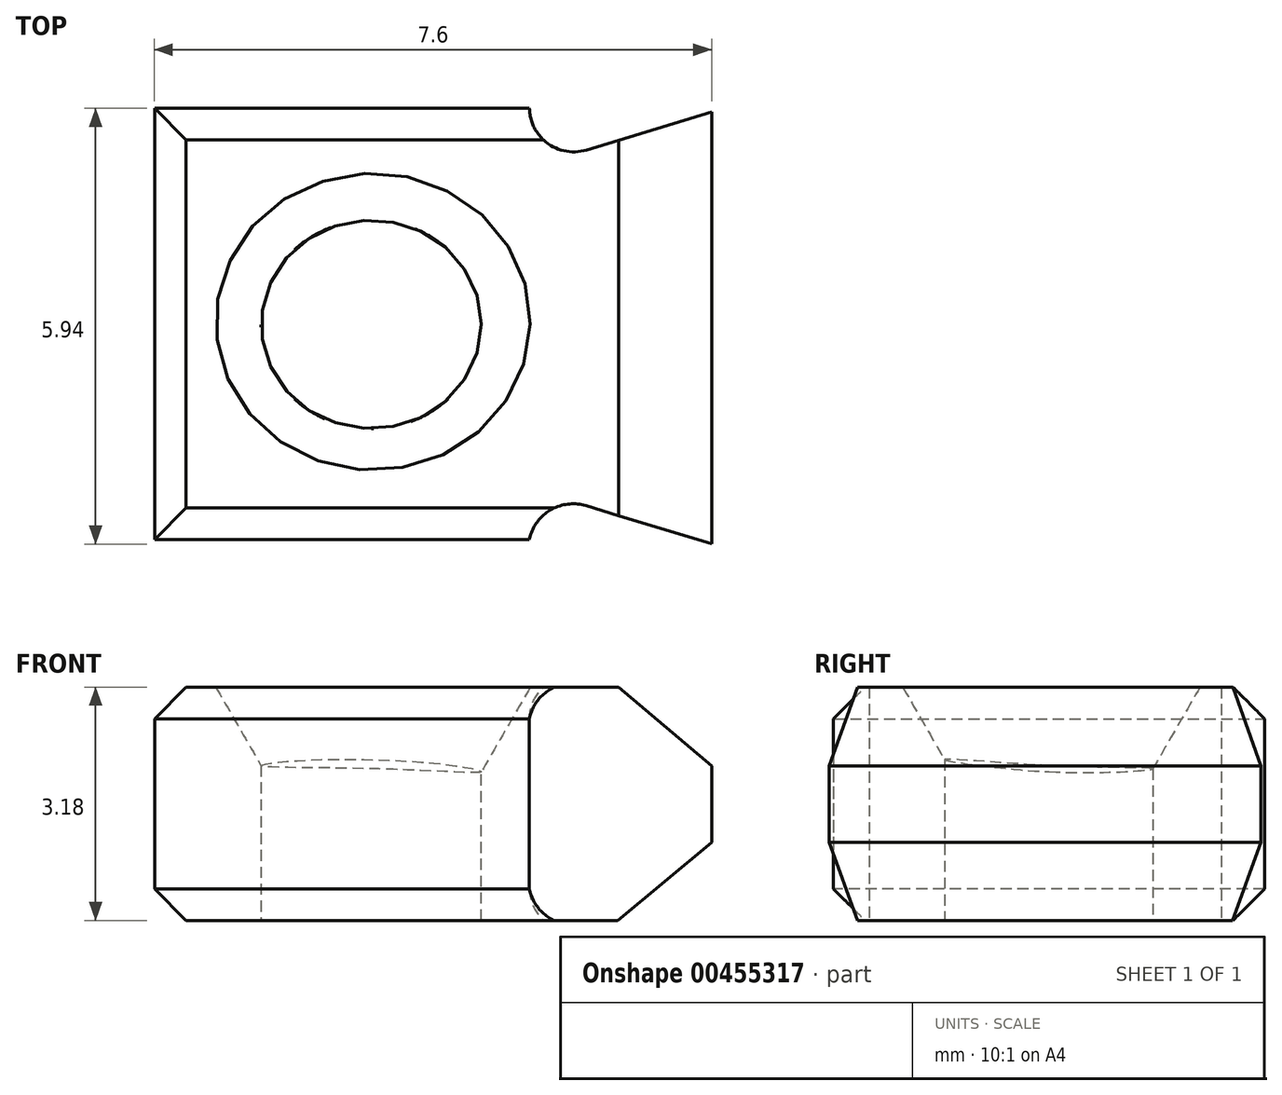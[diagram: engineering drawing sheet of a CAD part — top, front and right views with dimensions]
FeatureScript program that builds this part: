
annotation { "Feature Type Name" : "Feature", "Feature Type Description" : "" }
export const myFeature = defineFeature(function(context is Context, id is Id, definition is map)
    precondition{}
    {
        {
            var Q0;
            Q0=qCreatedBy(makeId("Top.planeOp"),FACE);
            var sketch = newSketch(context, id + "F0", { "sketchPlane" : qUnion([Q0])});
            skLineSegment(sketch, "E0.bottom", {"start": v(2.56, 2.94) * mm, "end": v(-2.56, 2.94) * mm});
            skLineSegment(sketch, "E0.top", {"start": v(2.56, -2.94) * mm, "end": v(-2.56, -2.94) * mm});
            skLineSegment(sketch, "E0.left", {"start": v(2.56, 2.94) * mm, "end": v(2.56, -2.94) * mm});
            skLineSegment(sketch, "E0.right", {"start": v(-2.56, 2.94) * mm, "end": v(-2.56, -2.94) * mm});
            skPoint(sketch, "E0.middle", {"position": v(0, 0) * mm});
            skLineSegment(sketch, "E1", {"start": v(5.04, 2.89) * mm, "end": v(5.04, -3) * mm});
            skLineSegment(sketch, "E2", {"start": v(5.04, 2.89) * mm, "end": v(3.34, 2.37) * mm});
            skLineSegment(sketch, "E3", {"start": v(5.04, -3) * mm, "end": v(3.32, -2.48) * mm});
            skArc(sketch, "E4", {"start": v(2.55, 2.94) * mm, "mid": v(2.8, 2.46) * mm, "end": v(3.34, 2.37) * mm});
            skArc(sketch, "E5", {"start": v(3.32, -2.48) * mm, "mid": v(2.84, -2.54) * mm, "end": v(2.56, -2.94) * mm});
            skSolve(sketch);
        }
        {
            var Q0;
            Q0=makeQuery(id+"F0.imprint","IMPRINT",FACE,{"disambiguationData":[TD([[makeQuery(id+"F0.imprint","IMPRINT",EDGE,{"derivedFrom":sQuery(id+"F0.wireOp",EDGE,"E0.bottom")}),1.0]])]});
            var Q1;
            Q1=makeQuery(id+"F0.imprint","IMPRINT",FACE,{"disambiguationData":[TD([[makeQuery(id+"F0.imprint","IMPRINT",EDGE,{"derivedFrom":sQuery(id+"F0.wireOp",EDGE,"E0.left")}),1.0]])]});
            extrude(context, id + "F1", {"entities" : qUnion([Q0, Q1]), "depth" : 3.18 * mm});
        }
        {
            var Q0;
            Q0=makeQuery(id+"F1.opExtrude","CAP_FACE",FACE,{"disambiguationData":[OSD([sQuery(id+"F0.wireOp",EDGE,"E0.bottom"),sQuery(id+"F0.wireOp",EDGE,"E0.top"),sQuery(id+"F0.wireOp",EDGE,"E0.right"),sQuery(id+"F0.wireOp",EDGE,"E1"),sQuery(id+"F0.wireOp",EDGE,"E2"),sQuery(id+"F0.wireOp",EDGE,"E3"),sQuery(id+"F0.wireOp",EDGE,"E4"),sQuery(id+"F0.wireOp",EDGE,"E5")])],"isStart":false});
            var sketch = newSketch(context, id + "F2", { "sketchPlane" : qUnion([Q0])});
            skEllipse(sketch, "E6", {"center": v(0.4, 0) * mm, "majorRadius": 1.5 * mm, "minorRadius": 1.42 * mm, "majorAxis": v(1, 0)});
            skSolve(sketch);
        }
        {
            var Q0;
            Q0=makeQuery(id+"F2.imprint","IMPRINT",FACE,{"disambiguationData":[TD([[makeQuery(id+"F2.imprint","IMPRINT",EDGE,{"derivedFrom":sQuery(id+"F2.wireOp",EDGE,"E6")}),1.0]])]});
            extrude(context, id + "F3", {"entities" : qUnion([Q0]), "operationType" : NewBodyOperationType.REMOVE, "endBound" : BoundingType.THROUGH_ALL, "oppositeDirection" : true, "depth" : 25 * mm});
        }
        {
            var Q0;
            Q0=makeQuery(id+"F1.opExtrude","CAP_FACE",FACE,{"disambiguationData":[OSD([sQuery(id+"F0.wireOp",EDGE,"E0.bottom"),sQuery(id+"F0.wireOp",EDGE,"E0.top"),sQuery(id+"F0.wireOp",EDGE,"E0.right"),sQuery(id+"F0.wireOp",EDGE,"E1"),sQuery(id+"F0.wireOp",EDGE,"E2"),sQuery(id+"F0.wireOp",EDGE,"E3"),sQuery(id+"F0.wireOp",EDGE,"E4"),sQuery(id+"F0.wireOp",EDGE,"E5")])],"isStart":false});
            var sketch = newSketch(context, id + "F4", { "sketchPlane" : qUnion([Q0])});
            skEllipse(sketch, "E7", {"center": v(0.42, 0.03) * mm, "majorRadius": 2.14 * mm, "minorRadius": 2.02 * mm, "majorAxis": v(1, 0)});
            skSolve(sketch);
        }
        {
            var Q0;
            Q0=qCreatedBy(makeId("Front.planeOp"),FACE);
            var sketch = newSketch(context, id + "F5", { "sketchPlane" : qUnion([Q0])});
            skLineSegment(sketch, "E8.0", {"start": v(1.07, 3.18) * mm, "end": v(2.57, 3.18) * mm});
            skLineSegment(sketch, "E9", {"start": v(1.87, 1.98) * mm, "end": v(2.57, 3.18) * mm});
            skLineSegment(sketch, "E10", {"start": v(1.87, 1.98) * mm, "end": v(1.07, 1.98) * mm});
            skLineSegment(sketch, "E11", {"start": v(1.07, 3.18) * mm, "end": v(1.07, 1.98) * mm});
            skPoint(sketch, "E12.orphan", {"position": v(-1.72, 3.18) * mm});
            skPoint(sketch, "E13.orphan", {"position": v(0.42, -0.53) * mm});
            skPoint(sketch, "E14.orphan", {"position": v(3.32, 4.49) * mm});
            skSolve(sketch);
        }
        {
            var Q0;
            Q0 = qSketchRegion(id + "F5", true);
            var Q1;
            Q1 = qConstructionFilter(qBodyType(qCreatedBy(id + "F4" ,EDGE), BodyType.WIRE), ConstructionObject.NO);
            sweep(context, id + "F6", {"operationType" : NewBodyOperationType.REMOVE, "profiles" : qUnion([Q0]), "path" : qUnion([Q1])});
        }
        {
            var Q0;
            Q0=makeQuery(id+"F1.opExtrude","SWEPT_FACE",FACE,{"disambiguationData":[OSD([sQuery(id+"F0.wireOp",EDGE,"E0.top")])]});
            var sketch = newSketch(context, id + "F7", { "sketchPlane" : qUnion([Q0])});
            skLineSegment(sketch, "E15.0.0", {"start": v(3.32, 0) * mm, "end": v(5.04, 0) * mm});
            skLineSegment(sketch, "E15.0.1", {"start": v(5.04, 0) * mm, "end": v(5.04, 3.18) * mm});
            skLineSegment(sketch, "E15.0.2", {"start": v(5.04, 3.18) * mm, "end": v(3.32, 3.18) * mm});
            skLineSegment(sketch, "E15.0.3", {"start": v(3.32, 3.18) * mm, "end": v(3.32, 0) * mm});
            skLineSegment(sketch, "E16.0.0", {"start": v(2.56, 0) * mm, "end": v(3.32, 0) * mm});
            skLineSegment(sketch, "E16.0.1", {"start": v(3.32, 0) * mm, "end": v(3.32, 3.18) * mm});
            skLineSegment(sketch, "E16.0.2", {"start": v(3.32, 3.18) * mm, "end": v(2.56, 3.18) * mm});
            skLineSegment(sketch, "E16.0.3", {"start": v(2.56, 3.18) * mm, "end": v(2.56, 0) * mm});
            skLineSegment(sketch, "E17.0.0", {"start": v(-2.56, 0) * mm, "end": v(2.56, 0) * mm});
            skLineSegment(sketch, "E17.0.1", {"start": v(2.56, 0) * mm, "end": v(2.56, 3.18) * mm});
            skLineSegment(sketch, "E17.0.2", {"start": v(2.56, 3.18) * mm, "end": v(-2.56, 3.18) * mm});
            skLineSegment(sketch, "E17.0.3", {"start": v(-2.56, 3.18) * mm, "end": v(-2.56, 0) * mm});
            skLineSegment(sketch, "E18", {"start": v(-2.56, 1.59) * mm, "end": v(5.04, 1.59) * mm});
            skLineSegment(sketch, "E19", {"start": v(5.04, 2.1) * mm, "end": v(3.77, 3.18) * mm});
            skLineSegment(sketch, "E20", {"start": v(5.04, 1.06) * mm, "end": v(3.76, 0) * mm});
            skSolve(sketch);
        }
        {
            var Q0;
            {var subQ3=sQuery(id+"F7.wireOp",EDGE,"E19");Q0=makeQuery(id+"F7.imprint","IMPRINT",FACE,{"disambiguationData":[TD([[makeQuery(id+"F7.imprint","IMPRINT",EDGE,{"derivedFrom":subQ3}),-1.0]])]});}
            var Q1;
            {var subQ3=sQuery(id+"F7.wireOp",EDGE,"E20");Q1=makeQuery(id+"F7.imprint","IMPRINT",FACE,{"disambiguationData":[TD([[makeQuery(id+"F7.imprint","IMPRINT",EDGE,{"derivedFrom":subQ3}),1.0]])]});}
            extrude(context, id + "F8", {"entities" : qUnion([Q0, Q1]), "operationType" : NewBodyOperationType.REMOVE, "endBound" : BoundingType.THROUGH_ALL, "oppositeDirection" : true, "depth" : 25 * mm, "hasSecondDirection" : true, "secondDirectionBound" : SecondDirectionBoundingType.THROUGH_ALL, "secondDirectionOppositeDirection" : false, "secondDirectionDepth" : 25 * mm});
        }
        {
            var Q0;
            Q0=makeQuery(id+"F1.opExtrude","CAP_EDGE",EDGE,{"disambiguationData":[OSD([sQuery(id+"F0.wireOp",EDGE,"E0.top")])],"isStart":false});
            var Q1;
            Q1=makeQuery(id+"F1.opExtrude","CAP_EDGE",EDGE,{"disambiguationData":[OSD([sQuery(id+"F0.wireOp",EDGE,"E0.right")])],"isStart":false});
            var Q2;
            Q2=makeQuery(id+"F1.opExtrude","CAP_EDGE",EDGE,{"disambiguationData":[OSD([sQuery(id+"F0.wireOp",EDGE,"E0.bottom")])],"isStart":false});
            var Q3;
            Q3=makeQuery(id+"F1.opExtrude","CAP_EDGE",EDGE,{"disambiguationData":[OSD([sQuery(id+"F0.wireOp",EDGE,"E0.right")])],"isStart":true});
            var Q4;
            Q4=makeQuery(id+"F1.opExtrude","CAP_EDGE",EDGE,{"disambiguationData":[OSD([sQuery(id+"F0.wireOp",EDGE,"E0.top")])],"isStart":true});
            var Q5;
            Q5=makeQuery(id+"F1.opExtrude","CAP_EDGE",EDGE,{"disambiguationData":[OSD([sQuery(id+"F0.wireOp",EDGE,"E0.bottom")])],"isStart":true});
            chamfer(context, id + "F9", {"entities" : qUnion([Q0, Q1, Q2, Q3, Q4, Q5]), "width" : .43 * mm, "tangentPropagation" : true});
        }
    });
